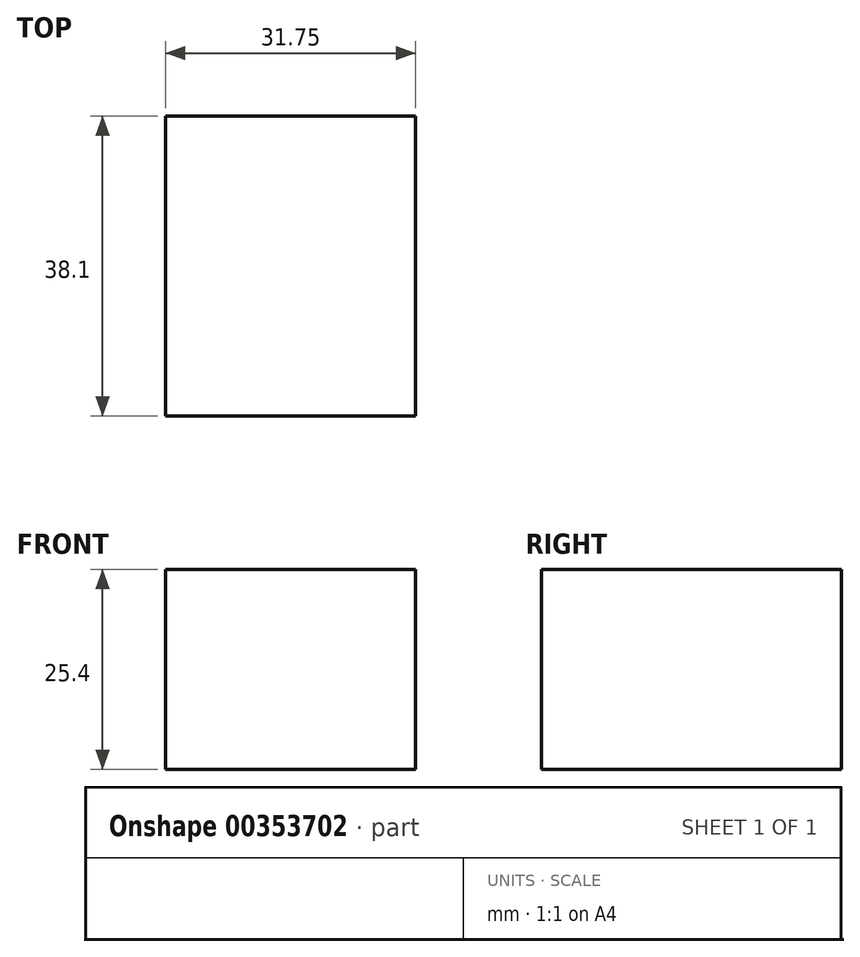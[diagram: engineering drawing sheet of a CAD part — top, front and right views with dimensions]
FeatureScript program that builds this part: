
annotation { "Feature Type Name" : "Feature", "Feature Type Description" : "" }
export const myFeature = defineFeature(function(context is Context, id is Id, definition is map)
    precondition{}
    {
        {
            var Q0;
            Q0=qCreatedBy(makeId("Front.planeOp"),FACE);
            var sketch = newSketch(context, id + "F0", { "sketchPlane" : qUnion([Q0])});
            skLineSegment(sketch, "E0", {"start": v(0, 0) * mm, "end": v(0, 25.4) * mm});
            skLineSegment(sketch, "E1", {"start": v(0, 25.4) * mm, "end": v(31.75, 25.4) * mm});
            skLineSegment(sketch, "E2", {"start": v(31.75, 25.4) * mm, "end": v(31.75, 0) * mm});
            skLineSegment(sketch, "E3", {"start": v(31.75, 0) * mm, "end": v(0, 0) * mm});
            skSolve(sketch);
        }
        {
            var Q0;
            Q0=makeQuery(id+"F0.imprint","IMPRINT",FACE,{"disambiguationData":[TD([[makeQuery(id+"F0.imprint","IMPRINT",EDGE,{"derivedFrom":sQuery(id+"F0.wireOp",EDGE,"E0")}),-1.0]])]});
            extrude(context, id + "F1", {"entities" : qUnion([Q0]), "depth" : 38.1 * mm});
        }
    });
